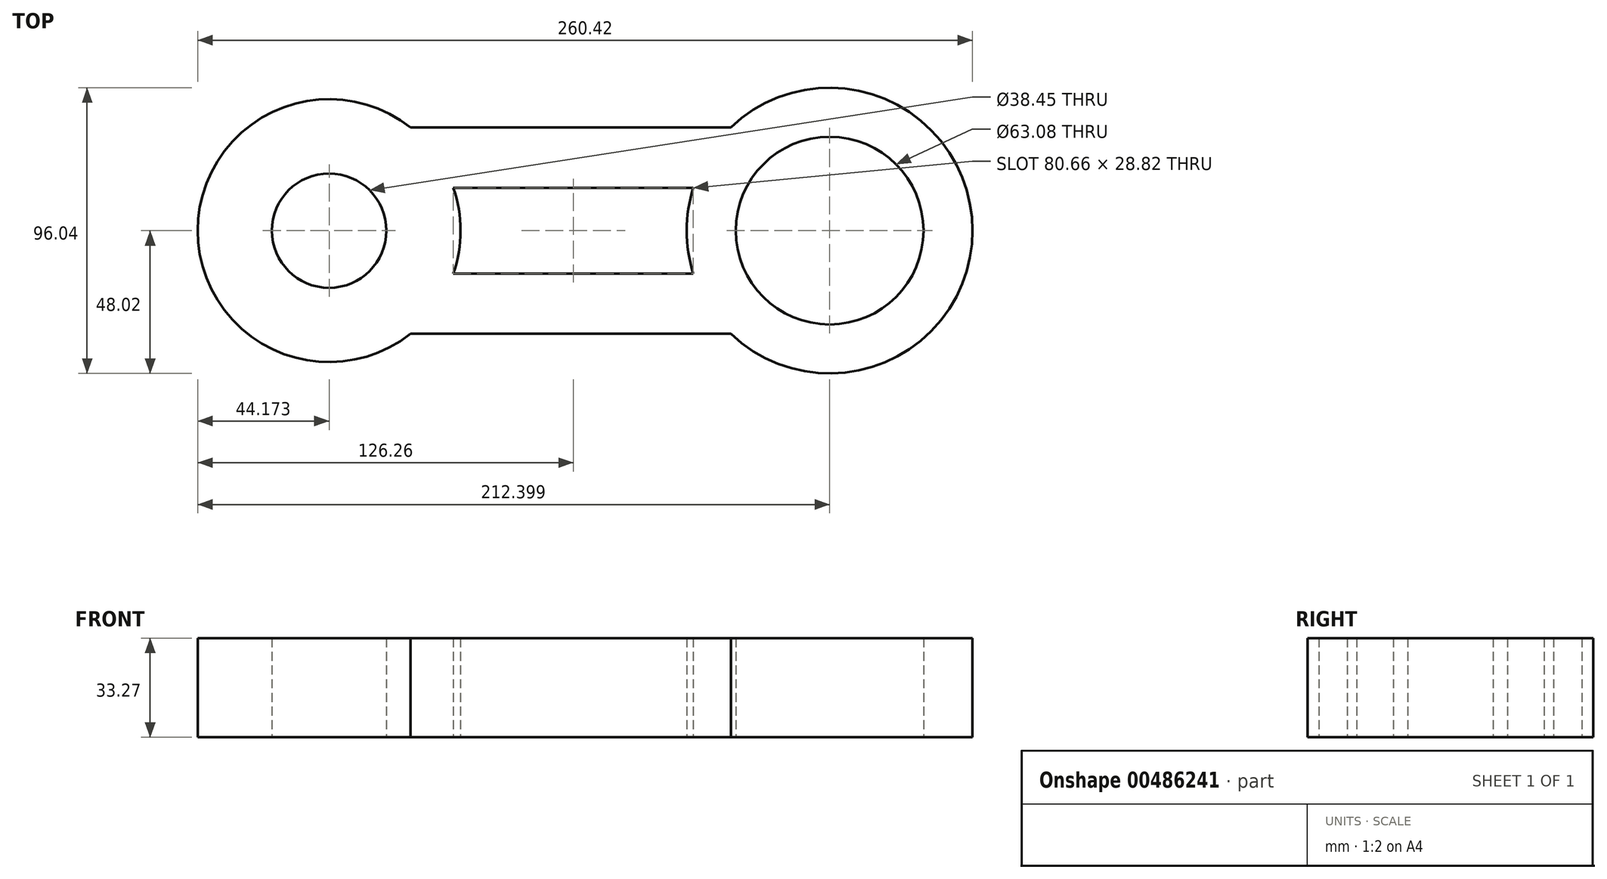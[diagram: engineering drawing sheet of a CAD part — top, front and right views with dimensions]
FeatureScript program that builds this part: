
annotation { "Feature Type Name" : "Feature", "Feature Type Description" : "" }
export const myFeature = defineFeature(function(context is Context, id is Id, definition is map)
    precondition{}
    {
        {
            var Q0;
            Q0=qCreatedBy(makeId("Top.planeOp"),FACE);
            var sketch = newSketch(context, id + "F0", { "sketchPlane" : qUnion([Q0])});
            skCircle(sketch, "E0", {"center": v(-130.66, 0) * mm, "radius": 44.17 * mm});
            skCircle(sketch, "E1", {"center": v(37.57, 0) * mm, "radius": 48.02 * mm});
            skCircle(sketch, "E2", {"center": v(-130.66, 0) * mm, "radius": 19.22 * mm});
            skCircle(sketch, "E3", {"center": v(37.57, 0) * mm, "radius": 31.54 * mm});
            skLineSegment(sketch, "E4", {"start": v(-88.9, -14.41) * mm, "end": v(-8.24, -14.41) * mm});
            skLineSegment(sketch, "E5", {"start": v(-8.24, 14.41) * mm, "end": v(-88.9, 14.41) * mm});
            skLineSegment(sketch, "E6", {"start": v(-103.29, 34.67) * mm, "end": v(4.34, 34.67) * mm});
            skLineSegment(sketch, "E7", {"start": v(4.34, 34.67) * mm, "end": v(4.34, -34.67) * mm});
            skLineSegment(sketch, "E8", {"start": v(-103.29, 34.67) * mm, "end": v(-103.29, -34.67) * mm});
            skLineSegment(sketch, "E9", {"start": v(-103.29, -34.67) * mm, "end": v(4.34, -34.67) * mm});
            skSolve(sketch);
        }
        {
            var Q0;
            {var subQ0=sQuery(id+"F0.wireOp",EDGE,"E4");Q0=makeQuery(id+"F0.imprint","IMPRINT",FACE,{"disambiguationData":[TD([[makeQuery(id+"F0.imprint","IMPRINT",EDGE,{"derivedFrom":subQ0}),-1.0]])]});}
            var Q1;
            {var subQ0=sQuery(id+"F0.wireOp",EDGE,"E5");Q1=makeQuery(id+"F0.imprint","IMPRINT",FACE,{"disambiguationData":[TD([[makeQuery(id+"F0.imprint","IMPRINT",EDGE,{"derivedFrom":subQ0}),-1.0]])]});}
            var Q2;
            {var subQ2=sQuery(id+"F0.wireOp",EDGE,"E7");Q2=makeQuery(id+"F0.imprint","IMPRINT",FACE,{"disambiguationData":[TD([[makeQuery(id+"F0.imprint","IMPRINT",EDGE,{"derivedFrom":subQ2}),-1.0]])]});}
            var Q3;
            {var subQ2=sQuery(id+"F0.wireOp",EDGE,"E8");Q3=makeQuery(id+"F0.imprint","IMPRINT",FACE,{"disambiguationData":[TD([[makeQuery(id+"F0.imprint","IMPRINT",EDGE,{"derivedFrom":subQ2}),1.0]])]});}
            var Q4;
            Q4=makeQuery(id+"F0.imprint","IMPRINT",FACE,{"disambiguationData":[TD([[makeQuery(id+"F0.imprint","IMPRINT",EDGE,{"derivedFrom":sQuery(id+"F0.wireOp",EDGE,"E2")}),-1.0]])]});
            var Q5;
            Q5=makeQuery(id+"F0.imprint","IMPRINT",FACE,{"disambiguationData":[TD([[makeQuery(id+"F0.imprint","IMPRINT",EDGE,{"derivedFrom":sQuery(id+"F0.wireOp",EDGE,"E3")}),-1.0]])]});
            extrude(context, id + "F1", {"entities" : qUnion([Q0, Q1, Q2, Q3, Q4, Q5]), "depth" : 33.27 * mm});
        }
    });
